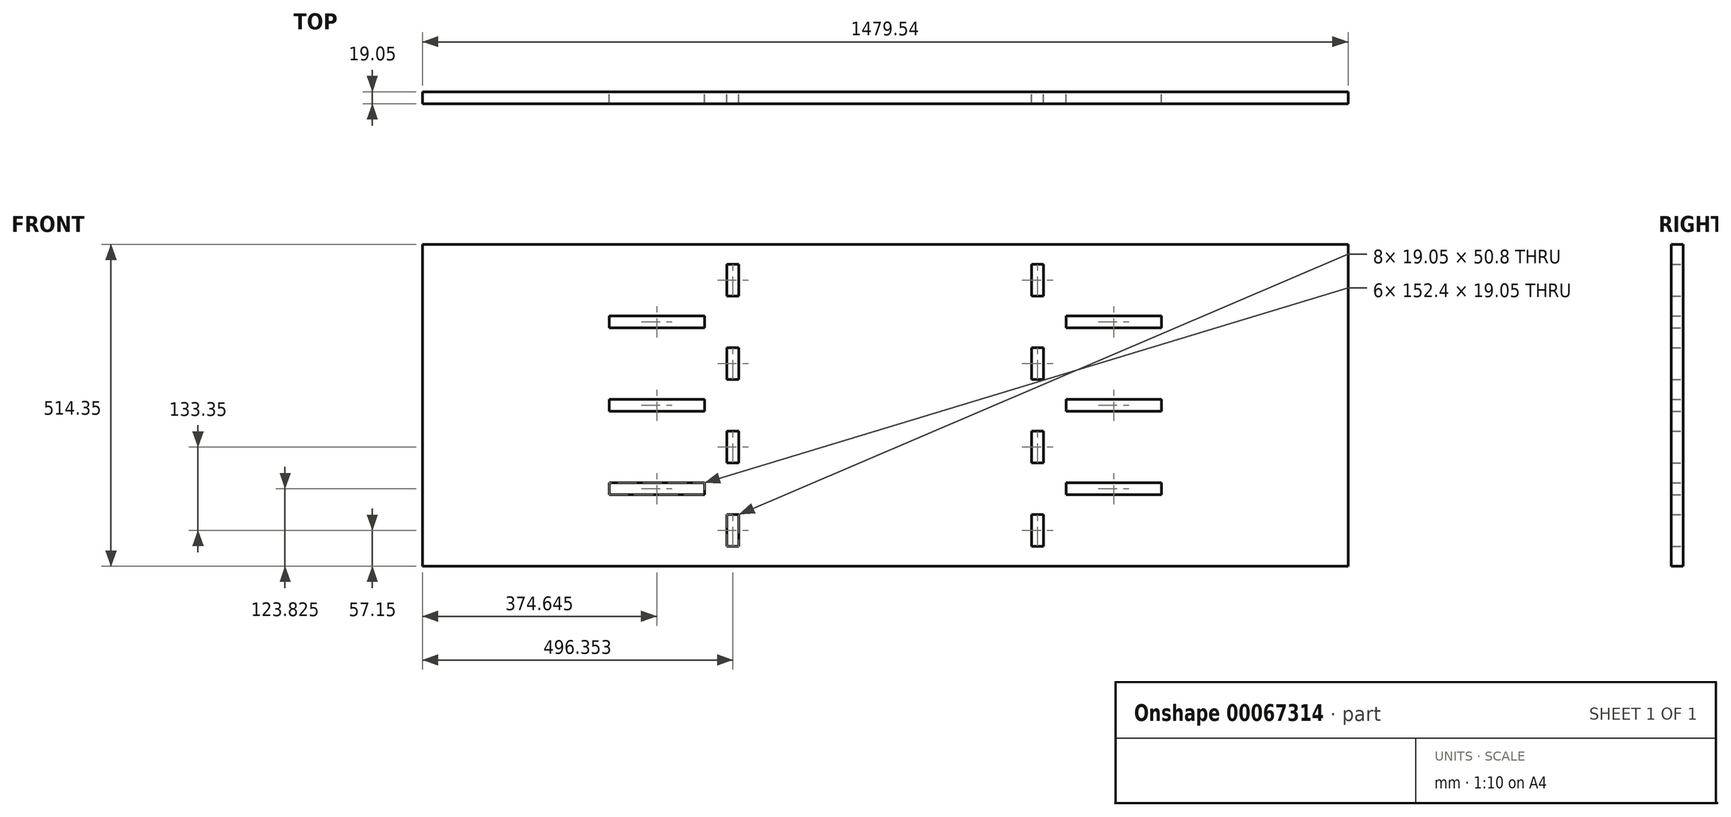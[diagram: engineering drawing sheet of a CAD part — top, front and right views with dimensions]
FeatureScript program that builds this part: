
annotation { "Feature Type Name" : "Feature", "Feature Type Description" : "" }
export const myFeature = defineFeature(function(context is Context, id is Id, definition is map)
    precondition{}
    {
        {
            var Q0;
            Q0=qCreatedBy(makeId("Front.planeOp"),FACE);
            var sketch = newSketch(context, id + "F0", { "sketchPlane" : qUnion([Q0])});
            skLineSegment(sketch, "E0.bottom", {"start": v(-739.77, 0) * mm, "end": v(739.78, 0) * mm});
            skLineSegment(sketch, "E0.top", {"start": v(-739.78, -514.35) * mm, "end": v(739.78, -514.35) * mm});
            skLineSegment(sketch, "E0.left", {"start": v(-739.78, 0) * mm, "end": v(-739.78, -514.35) * mm});
            skLineSegment(sketch, "E0.right", {"start": v(739.78, 0) * mm, "end": v(739.78, -514.35) * mm});
            skLineSegment(sketch, "E1.left", {"start": v(-252.94, -165.1) * mm, "end": v(-252.94, -215.9) * mm});
            skLineSegment(sketch, "E2.bottom", {"start": v(-441.33, -381) * mm, "end": v(-288.93, -381) * mm});
            skLineSegment(sketch, "E2.top", {"start": v(-441.33, -400.05) * mm, "end": v(-288.93, -400.05) * mm});
            skLineSegment(sketch, "E3.left", {"start": v(-252.94, -431.8) * mm, "end": v(-252.94, -482.6) * mm});
            skLineSegment(sketch, "E4.right", {"start": v(-233.9, -31.75) * mm, "end": v(-233.9, -82.55) * mm});
            skLineSegment(sketch, "E5.right", {"start": v(252.94, -298.45) * mm, "end": v(252.94, -349.25) * mm});
            skLineSegment(sketch, "E6.bottom", {"start": v(-441.32, -247.65) * mm, "end": v(-288.93, -247.65) * mm});
            skLineSegment(sketch, "E6.top", {"start": v(-441.33, -266.7) * mm, "end": v(-288.93, -266.7) * mm});
            skLineSegment(sketch, "E7.bottom", {"start": v(-441.32, -114.3) * mm, "end": v(-288.93, -114.3) * mm});
            skLineSegment(sketch, "E7.top", {"start": v(-441.32, -133.35) * mm, "end": v(-288.93, -133.35) * mm});
            skLineSegment(sketch, "E8.left", {"start": v(233.9, -31.75) * mm, "end": v(233.9, -82.55) * mm});
            skLineSegment(sketch, "E9.right", {"start": v(252.94, -431.8) * mm, "end": v(252.94, -482.6) * mm});
            skLineSegment(sketch, "E1.right", {"start": v(-233.9, -165.1) * mm, "end": v(-233.9, -215.9) * mm});
            skLineSegment(sketch, "E3.right", {"start": v(-233.9, -431.8) * mm, "end": v(-233.9, -482.6) * mm});
            skLineSegment(sketch, "E10.bottom", {"start": v(288.92, -381) * mm, "end": v(441.32, -381) * mm});
            skLineSegment(sketch, "E8.right", {"start": v(252.94, -31.75) * mm, "end": v(252.94, -82.55) * mm});
            skLineSegment(sketch, "E11.bottom", {"start": v(288.92, -247.65) * mm, "end": v(441.32, -247.65) * mm});
            skLineSegment(sketch, "E10.top", {"start": v(288.92, -400.05) * mm, "end": v(441.32, -400.05) * mm});
            skLineSegment(sketch, "E9.left", {"start": v(233.9, -431.8) * mm, "end": v(233.9, -482.6) * mm});
            skLineSegment(sketch, "E12.bottom", {"start": v(288.92, -114.3) * mm, "end": v(441.32, -114.3) * mm});
            skLineSegment(sketch, "E11.top", {"start": v(288.92, -266.7) * mm, "end": v(441.32, -266.7) * mm});
            skLineSegment(sketch, "E12.top", {"start": v(288.92, -133.35) * mm, "end": v(441.32, -133.35) * mm});
            skLineSegment(sketch, "E4.left", {"start": v(-252.94, -31.75) * mm, "end": v(-252.94, -82.55) * mm});
            skLineSegment(sketch, "E5.left", {"start": v(233.9, -298.45) * mm, "end": v(233.9, -349.25) * mm});
            skLineSegment(sketch, "E13.left", {"start": v(-252.94, -298.45) * mm, "end": v(-252.94, -349.25) * mm});
            skLineSegment(sketch, "E14.right", {"start": v(252.94, -165.1) * mm, "end": v(252.94, -215.9) * mm});
            skLineSegment(sketch, "E13.right", {"start": v(-233.9, -298.45) * mm, "end": v(-233.9, -349.25) * mm});
            skLineSegment(sketch, "E14.left", {"start": v(233.9, -165.1) * mm, "end": v(233.9, -215.9) * mm});
            skLineSegment(sketch, "E2.left", {"start": v(-441.33, -381) * mm, "end": v(-441.33, -400.05) * mm});
            skLineSegment(sketch, "E11.right", {"start": v(441.32, -247.65) * mm, "end": v(441.32, -266.7) * mm});
            skLineSegment(sketch, "E2.right", {"start": v(-288.93, -381) * mm, "end": v(-288.93, -400.05) * mm});
            skLineSegment(sketch, "E14.bottom", {"start": v(233.9, -165.1) * mm, "end": v(252.94, -165.1) * mm});
            skLineSegment(sketch, "E9.bottom", {"start": v(233.9, -431.8) * mm, "end": v(252.94, -431.8) * mm});
            skLineSegment(sketch, "E6.left", {"start": v(-441.33, -247.65) * mm, "end": v(-441.33, -266.7) * mm});
            skLineSegment(sketch, "E6.right", {"start": v(-288.93, -247.65) * mm, "end": v(-288.93, -266.7) * mm});
            skLineSegment(sketch, "E7.left", {"start": v(-441.32, -114.3) * mm, "end": v(-441.32, -133.35) * mm});
            skLineSegment(sketch, "E7.right", {"start": v(-288.93, -114.3) * mm, "end": v(-288.93, -133.35) * mm});
            skLineSegment(sketch, "E10.left", {"start": v(288.92, -381) * mm, "end": v(288.92, -400.05) * mm});
            skLineSegment(sketch, "E12.right", {"start": v(441.32, -114.3) * mm, "end": v(441.32, -133.35) * mm});
            skLineSegment(sketch, "E14.top", {"start": v(233.9, -215.9) * mm, "end": v(252.94, -215.9) * mm});
            skLineSegment(sketch, "E8.bottom", {"start": v(233.9, -31.75) * mm, "end": v(252.94, -31.75) * mm});
            skLineSegment(sketch, "E10.right", {"start": v(441.32, -381) * mm, "end": v(441.32, -400.05) * mm});
            skLineSegment(sketch, "E13.bottom", {"start": v(-252.94, -298.45) * mm, "end": v(-233.9, -298.45) * mm});
            skLineSegment(sketch, "E4.bottom", {"start": v(-252.94, -31.75) * mm, "end": v(-233.9, -31.75) * mm});
            skLineSegment(sketch, "E5.bottom", {"start": v(233.9, -298.45) * mm, "end": v(252.94, -298.45) * mm});
            skLineSegment(sketch, "E8.top", {"start": v(233.9, -82.55) * mm, "end": v(252.94, -82.55) * mm});
            skLineSegment(sketch, "E13.top", {"start": v(-252.94, -349.25) * mm, "end": v(-233.9, -349.25) * mm});
            skLineSegment(sketch, "E1.bottom", {"start": v(-252.94, -165.1) * mm, "end": v(-233.9, -165.1) * mm});
            skLineSegment(sketch, "E3.bottom", {"start": v(-252.94, -431.8) * mm, "end": v(-233.9, -431.8) * mm});
            skLineSegment(sketch, "E12.left", {"start": v(288.92, -114.3) * mm, "end": v(288.92, -133.35) * mm});
            skLineSegment(sketch, "E4.top", {"start": v(-252.94, -82.55) * mm, "end": v(-233.9, -82.55) * mm});
            skLineSegment(sketch, "E5.top", {"start": v(233.9, -349.25) * mm, "end": v(252.94, -349.25) * mm});
            skLineSegment(sketch, "E11.left", {"start": v(288.92, -247.65) * mm, "end": v(288.92, -266.7) * mm});
            skLineSegment(sketch, "E1.top", {"start": v(-252.94, -215.9) * mm, "end": v(-233.9, -215.9) * mm});
            skLineSegment(sketch, "E15", {"start": v(233.9, -482.6) * mm, "end": v(252.94, -482.6) * mm});
            skLineSegment(sketch, "E16", {"start": v(-252.94, -482.6) * mm, "end": v(-233.9, -482.6) * mm});
            skLineSegment(sketch, "E17.bottom", {"start": v(-511.17, 0) * mm, "end": v(-358.77, 0) * mm});
            skLineSegment(sketch, "E17.top", {"start": v(-511.17, 19.05) * mm, "end": v(-358.77, 19.05) * mm});
            skLineSegment(sketch, "E17.left", {"start": v(-511.17, 0) * mm, "end": v(-511.17, 19.05) * mm});
            skLineSegment(sketch, "E17.right", {"start": v(-358.77, 0) * mm, "end": v(-358.77, 19.05) * mm});
            skLineSegment(sketch, "E18.bottom", {"start": v(358.78, 0) * mm, "end": v(511.18, 0) * mm});
            skLineSegment(sketch, "E18.top", {"start": v(358.78, 19.05) * mm, "end": v(511.18, 19.05) * mm});
            skLineSegment(sketch, "E18.left", {"start": v(358.78, 0) * mm, "end": v(358.78, 19.05) * mm});
            skLineSegment(sketch, "E18.right", {"start": v(511.18, 0) * mm, "end": v(511.18, 19.05) * mm});
            skLineSegment(sketch, "E19.bottom", {"start": v(-511.18, -514.35) * mm, "end": v(-358.78, -514.35) * mm});
            skLineSegment(sketch, "E19.top", {"start": v(-511.18, -533.4) * mm, "end": v(-358.78, -533.4) * mm});
            skLineSegment(sketch, "E19.left", {"start": v(-511.18, -514.35) * mm, "end": v(-511.18, -533.4) * mm});
            skLineSegment(sketch, "E19.right", {"start": v(-358.78, -514.35) * mm, "end": v(-358.78, -533.4) * mm});
            skLineSegment(sketch, "E20.bottom", {"start": v(358.78, -514.35) * mm, "end": v(511.18, -514.35) * mm});
            skLineSegment(sketch, "E20.top", {"start": v(358.78, -533.4) * mm, "end": v(511.18, -533.4) * mm});
            skLineSegment(sketch, "E20.left", {"start": v(358.78, -514.35) * mm, "end": v(358.78, -533.4) * mm});
            skLineSegment(sketch, "E20.right", {"start": v(511.18, -514.35) * mm, "end": v(511.18, -533.4) * mm});
            skSolve(sketch);
        }
        {
            var Q0;
            Q0=makeQuery(id+"F0.imprint","IMPRINT",FACE,{"disambiguationData":[TD([[makeQuery(id+"F0.imprint","IMPRINT",EDGE,{"derivedFrom":sQuery(id+"F0.wireOp",EDGE,"E0.bottom")}),-1.0]])]});
            var Q1;
            Q1=makeQuery(id+"F0.imprint","IMPRINT",FACE,{"disambiguationData":[TD([[makeQuery(id+"F0.imprint","IMPRINT",EDGE,{"derivedFrom":sQuery(id+"F0.wireOp",EDGE,"E17.bottom")}),1.0]])]});
            var Q2;
            Q2=makeQuery(id+"F0.imprint","IMPRINT",FACE,{"disambiguationData":[TD([[makeQuery(id+"F0.imprint","IMPRINT",EDGE,{"derivedFrom":sQuery(id+"F0.wireOp",EDGE,"9f5a9505-6058-4a8e-9ba1-026463f0cc64.bottom")}),1.0]])]});
            var Q3;
            Q3=makeQuery(id+"F0.imprint","IMPRINT",FACE,{"disambiguationData":[TD([[makeQuery(id+"F0.imprint","IMPRINT",EDGE,{"derivedFrom":sQuery(id+"F0.wireOp",EDGE,"E18.bottom")}),1.0]])]});
            var Q4;
            Q4=makeQuery(id+"F0.imprint","IMPRINT",FACE,{"disambiguationData":[TD([[makeQuery(id+"F0.imprint","IMPRINT",EDGE,{"derivedFrom":sQuery(id+"F0.wireOp",EDGE,"E19.bottom")}),-1.0]])]});
            var Q5;
            Q5=makeQuery(id+"F0.imprint","IMPRINT",FACE,{"disambiguationData":[TD([[makeQuery(id+"F0.imprint","IMPRINT",EDGE,{"derivedFrom":sQuery(id+"F0.wireOp",EDGE,"E20.bottom")}),-1.0]])]});
            extrude(context, id + "F1", {"entities" : qUnion([Q0, Q1, Q2, Q3, Q4, Q5]), "depth" : 19.05 * mm});
        }
    });
